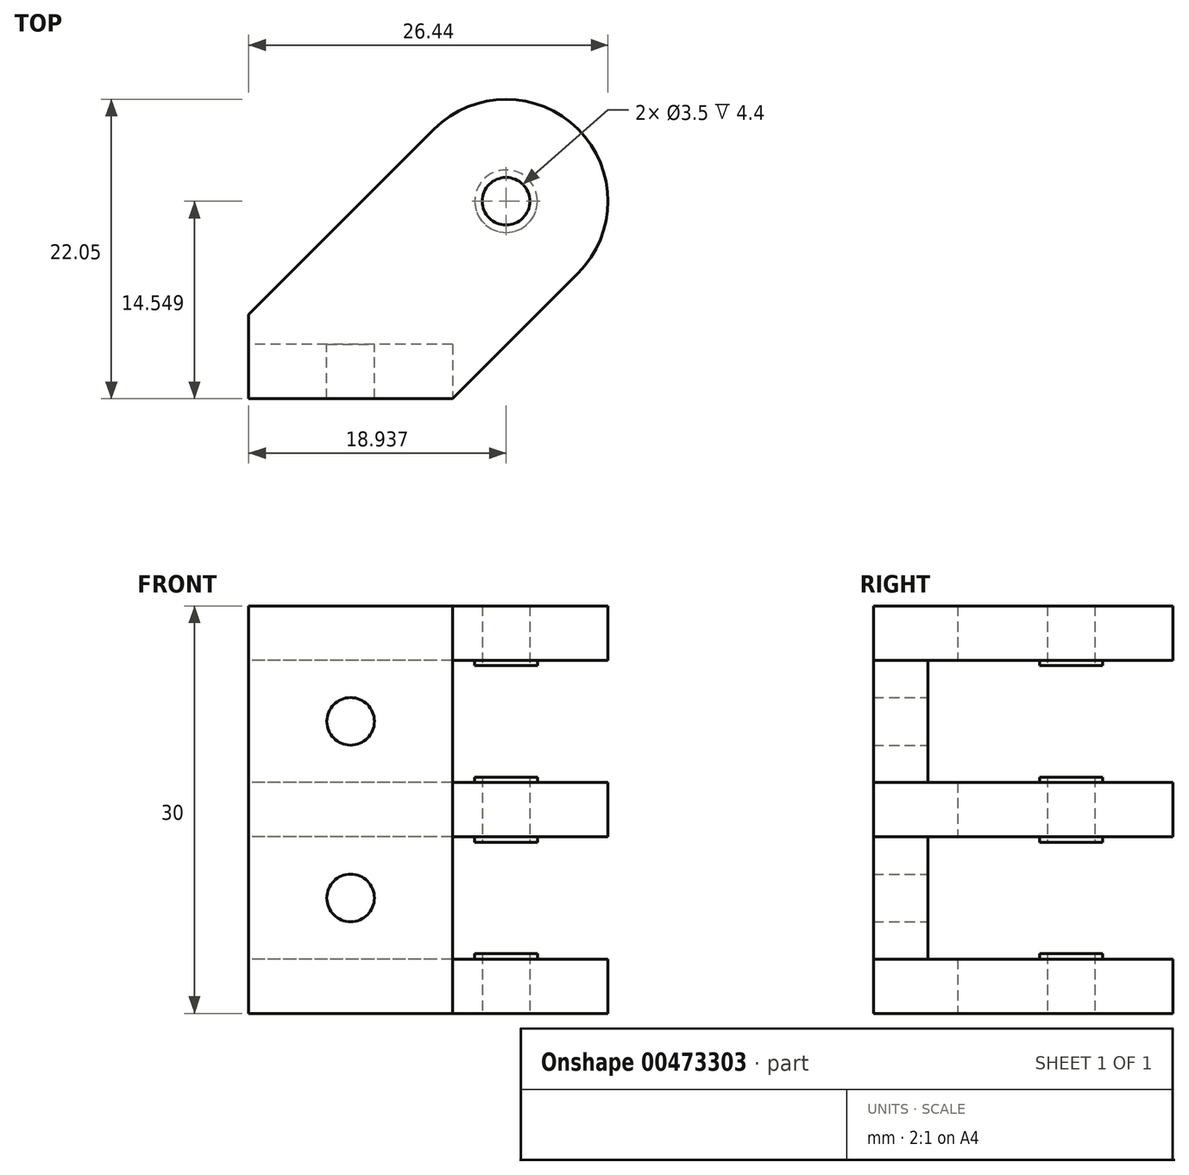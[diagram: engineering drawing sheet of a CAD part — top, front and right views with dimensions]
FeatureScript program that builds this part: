
annotation { "Feature Type Name" : "Feature", "Feature Type Description" : "" }
export const myFeature = defineFeature(function(context is Context, id is Id, definition is map)
    precondition{}
    {
        {
            var Q0;
            Q0=qCreatedBy(makeId("Top.planeOp"),FACE);
            var sketch = newSketch(context, id + "F0", { "sketchPlane" : qUnion([Q0])});
            skLineSegment(sketch, "E0.top", {"start": v(2.18, -5.35) * mm, "end": v(-15.04, -5.35) * mm});
            skLineSegment(sketch, "E0.right", {"start": v(-15.04, -1.35) * mm, "end": v(-15.04, -5.35) * mm});
            skCircle(sketch, "E1", {"center": v(6.12, 9.2) * mm, "radius": 1.75 * mm});
            skArc(sketch, "E2", {"start": v(11.42, 3.9) * mm, "mid": v(11.42, 14.5) * mm, "end": v(0.81, 14.5) * mm});
            skLineSegment(sketch, "E3", {"start": v(11.42, 3.9) * mm, "end": v(2.18, -5.35) * mm});
            skLineSegment(sketch, "E4", {"start": v(0.81, 14.5) * mm, "end": v(-15.04, -1.35) * mm});
            skSolve(sketch);
        }
        {
            var Q0;
            Q0 = qSketchRegion(id + "F0", true);
            extrude(context, id + "F1", {"entities" : qUnion([Q0]), "depth" : 30 * mm, "offsetDistance" : 25 * mm});
        }
        {
            var Q0;
            Q0=makeQuery(id+"F1.opExtrude","SWEPT_FACE",FACE,{"disambiguationData":[OSD([sQuery(id+"F0.wireOp",EDGE,"E0.right")])]});
            var sketch = newSketch(context, id + "F2", { "sketchPlane" : qUnion([Q0])});
            skLineSegment(sketch, "E5.bottom", {"start": v(1.35, 4) * mm, "end": v(-21.72, 4) * mm});
            skLineSegment(sketch, "E5.top", {"start": v(1.35, 13) * mm, "end": v(-21.72, 13) * mm});
            skLineSegment(sketch, "E5.left", {"start": v(1.35, 4) * mm, "end": v(1.35, 13) * mm});
            skLineSegment(sketch, "E5.right", {"start": v(-21.72, 4) * mm, "end": v(-21.72, 13) * mm});
            skLineSegment(sketch, "E6.bottom", {"start": v(1.35, 17) * mm, "end": v(-26.4, 17) * mm});
            skLineSegment(sketch, "E6.top", {"start": v(1.35, 26) * mm, "end": v(-26.4, 26) * mm});
            skLineSegment(sketch, "E6.left", {"start": v(1.35, 17) * mm, "end": v(1.35, 26) * mm});
            skLineSegment(sketch, "E6.right", {"start": v(-26.4, 17) * mm, "end": v(-26.4, 26) * mm});
            skSolve(sketch);
        }
        {
            var Q0;
            Q0 = qSketchRegion(id + "F2", true);
            extrude(context, id + "F3", {"entities" : qUnion([Q0]), "operationType" : NewBodyOperationType.REMOVE, "oppositeDirection" : true, "depth" : 39.1 * mm, "offsetDistance" : 25 * mm});
        }
        {
            var Q0;
            Q0=makeQuery(id+"F1.opExtrude","CAP_FACE",FACE,{"disambiguationData":[OSD([sQuery(id+"F0.wireOp",EDGE,"E0.top"),sQuery(id+"F0.wireOp",EDGE,"E0.right"),sQuery(id+"F0.wireOp",EDGE,"E1"),sQuery(id+"F0.wireOp",EDGE,"E2"),sQuery(id+"F0.wireOp",EDGE,"E3"),sQuery(id+"F0.wireOp",EDGE,"E4")])],"isStart":false});
            var sketch = newSketch(context, id + "F4", { "sketchPlane" : qUnion([Q0])});
            skLineSegment(sketch, "E7.bottom", {"start": v(-15.04, 10.99) * mm, "end": v(-12.82, 10.99) * mm});
            skLineSegment(sketch, "E7.top", {"start": v(-15.04, -5.35) * mm, "end": v(-12.82, -5.35) * mm});
            skLineSegment(sketch, "E7.left", {"start": v(-15.04, 10.99) * mm, "end": v(-15.04, -5.35) * mm});
            skLineSegment(sketch, "E7.right", {"start": v(-12.82, 10.99) * mm, "end": v(-12.82, -5.35) * mm});
            skSolve(sketch);
        }
        {
            var Q0;
            Q0 = qSketchRegion(id + "F4", true);
            extrude(context, id + "F5", {"entities" : qUnion([Q0]), "operationType" : NewBodyOperationType.REMOVE, "oppositeDirection" : true, "depth" : 500 * mm, "offsetDistance" : 25 * mm});
        }
        {
            var Q0;
            Q0=makeQuery(id+"F3.boolean.opBoolean","COPY",FACE,{"derivedFrom":makeQuery(id+"F3.opExtrude","SWEPT_FACE",FACE,{"disambiguationData":[OSD([sQuery(id+"F2.wireOp",EDGE,"E5.top")])]})});
            var sketch = newSketch(context, id + "F6", { "sketchPlane" : qUnion([Q0])});
            skCircle(sketch, "E8", {"center": v(6.12, -9.2) * mm, "radius": 2.3 * mm});
            skCircle(sketch, "E9.0", {"center": v(6.12, -9.2) * mm, "radius": 1.75 * mm});
            skSolve(sketch);
        }
        {
            var Q0;
            Q0 = qSketchRegion(id + "F6", true);
            extrude(context, id + "F7", {"entities" : qUnion([Q0]), "operationType" : NewBodyOperationType.ADD, "depth" : 0.4 * mm, "offsetDistance" : 25 * mm});
        }
        {
            var Q0;
            Q0=makeQuery(id+"F3.boolean.opBoolean","COPY",FACE,{"derivedFrom":makeQuery(id+"F3.opExtrude","SWEPT_FACE",FACE,{"disambiguationData":[OSD([sQuery(id+"F2.wireOp",EDGE,"E6.top")])]})});
            var sketch = newSketch(context, id + "F8", { "sketchPlane" : qUnion([Q0])});
            skCircle(sketch, "E10.0", {"center": v(6.12, -9.2) * mm, "radius": 2.3 * mm});
            skCircle(sketch, "E11.0", {"center": v(6.12, -9.2) * mm, "radius": 1.75 * mm});
            skSolve(sketch);
        }
        {
            var Q0;
            Q0 = qSketchRegion(id + "F8", true);
            extrude(context, id + "F9", {"entities" : qUnion([Q0]), "operationType" : NewBodyOperationType.ADD, "depth" : 0.4 * mm, "offsetDistance" : 25 * mm});
        }
        {
            var Q0;
            Q0=makeQuery(id+"F3.boolean.opBoolean","COPY",FACE,{"derivedFrom":makeQuery(id+"F3.opExtrude","SWEPT_FACE",FACE,{"disambiguationData":[OSD([sQuery(id+"F2.wireOp",EDGE,"E6.bottom")])]})});
            var sketch = newSketch(context, id + "F10", { "sketchPlane" : qUnion([Q0])});
            skCircle(sketch, "E12.0.0", {"center": v(6.12, 9.2) * mm, "radius": 2.3 * mm});
            skCircle(sketch, "E13.0", {"center": v(6.12, 9.2) * mm, "radius": 1.75 * mm});
            skSolve(sketch);
        }
        {
            var Q0;
            Q0 = qSketchRegion(id + "F10", true);
            extrude(context, id + "F11", {"entities" : qUnion([Q0]), "operationType" : NewBodyOperationType.ADD, "depth" : 0.4 * mm, "offsetDistance" : 25 * mm});
        }
        {
            var Q0;
            Q0=makeQuery(id+"F3.boolean.opBoolean","COPY",FACE,{"derivedFrom":makeQuery(id+"F3.opExtrude","SWEPT_FACE",FACE,{"disambiguationData":[OSD([sQuery(id+"F2.wireOp",EDGE,"E5.bottom")])]})});
            var sketch = newSketch(context, id + "F12", { "sketchPlane" : qUnion([Q0])});
            skCircle(sketch, "E14.0", {"center": v(6.12, 9.2) * mm, "radius": 2.3 * mm});
            skCircle(sketch, "E15.0", {"center": v(6.12, 9.2) * mm, "radius": 1.75 * mm});
            skSolve(sketch);
        }
        {
            var Q0;
            Q0 = qSketchRegion(id + "F12", true);
            extrude(context, id + "F13", {"entities" : qUnion([Q0]), "operationType" : NewBodyOperationType.ADD, "depth" : 0.4 * mm, "offsetDistance" : 25 * mm});
        }
        {
            var Q0;
            Q0=makeQuery(id+"F1.opExtrude","SWEPT_FACE",FACE,{"disambiguationData":[OSD([sQuery(id+"F0.wireOp",EDGE,"E0.top")])]});
            var sketch = newSketch(context, id + "F14", { "sketchPlane" : qUnion([Q0])});
            skPoint(sketch, "E16.0", {"position": v(6.18, 26) * mm});
            skPoint(sketch, "E17.0", {"position": v(6.18, 17) * mm});
            skPoint(sketch, "E18.0", {"position": v(6.18, 13) * mm});
            skPoint(sketch, "E19.0", {"position": v(6.18, 4) * mm});
            skLineSegment(sketch, "E20.bottom", {"start": v(6.18, 13) * mm, "end": v(2.18, 13) * mm});
            skLineSegment(sketch, "E20.top", {"start": v(6.18, 4) * mm, "end": v(2.18, 4) * mm});
            skLineSegment(sketch, "E20.left", {"start": v(6.18, 13) * mm, "end": v(6.18, 4) * mm});
            skLineSegment(sketch, "E20.right", {"start": v(2.18, 13) * mm, "end": v(2.18, 4) * mm});
            skLineSegment(sketch, "E21.bottom", {"start": v(6.18, 17) * mm, "end": v(2.18, 17) * mm});
            skLineSegment(sketch, "E21.top", {"start": v(6.18, 26) * mm, "end": v(2.18, 26) * mm});
            skLineSegment(sketch, "E21.left", {"start": v(6.18, 17) * mm, "end": v(6.18, 26) * mm});
            skLineSegment(sketch, "E21.right", {"start": v(2.18, 17) * mm, "end": v(2.18, 26) * mm});
            skSolve(sketch);
        }
        {
            var Q0;
            Q0 = qSketchRegion(id + "F14", true);
            extrude(context, id + "F15", {"entities" : qUnion([Q0]), "operationType" : NewBodyOperationType.REMOVE, "oppositeDirection" : true, "depth" : 6 * mm, "offsetDistance" : 25 * mm});
        }
        {
            var Q0;
            Q0=makeQuery(id+"F3.boolean.opBoolean","COPY",FACE,{"derivedFrom":makeQuery(id+"F3.opExtrude","SWEPT_FACE",FACE,{"disambiguationData":[OSD([sQuery(id+"F2.wireOp",EDGE,"E6.left")])]})});
            var sketch = newSketch(context, id + "F16", { "sketchPlane" : qUnion([Q0])});
            skCircle(sketch, "E22", {"center": v(5.32, 21.5) * mm, "radius": 1.75 * mm});
            skPoint(sketch, "E22.centerSnap0", {"position": v(5.32, 26) * mm});
            skPoint(sketch, "E22.centerSnap1", {"position": v(-2.18, 21.5) * mm});
            skPoint(sketch, "E23.0", {"position": v(5.32, 13) * mm});
            skPoint(sketch, "E24.0", {"position": v(-2.18, 8.5) * mm});
            skCircle(sketch, "E25", {"center": v(5.32, 8.5) * mm, "radius": 1.75 * mm});
            skSolve(sketch);
        }
        {
            var Q0;
            Q0 = qSketchRegion(id + "F16", true);
            extrude(context, id + "F17", {"entities" : qUnion([Q0]), "operationType" : NewBodyOperationType.REMOVE, "oppositeDirection" : true, "depth" : 25 * mm, "offsetDistance" : 25 * mm});
        }
    });
